FCSTD DOCUMENT  (FreeCAD 0.19R21911 +2545 (Git))
Label: zawieszenie
License: All rights reserved
LicenseURL: http://en.wikipedia.org/wiki/All_rights_reserved
objects: App::Link×4, App::FeaturePython×2, Part::FeaturePython×2
note: 1 computed .brp shape members not serialized (recipe doc carries the construction recipe); baked Part::Feature solids carry a one-line shape summary decoded from their .brp
EXTERNAL_REF file=zawieszenie-dol.fcstd obj=Assembly
EXTERNAL_REF file=zawieszenia-gora.fcstd obj=Assembly

FEATURE [App::FeaturePython] Constraints  # WARN: FeaturePython — macro-defined, semantics opaque (R4)
  _LinkVersion = 1
  _Version = 1
FEATURE [App::FeaturePython] Elements  # WARN: FeaturePython — macro-defined, semantics opaque (R4)
  _LinkVersion = 1
FEATURE [App::Link] Link  label="Link_zawieszenie-dol"
  LinkPlacement = pos=(0.000376772,73.4466,183.14) rot=(0,0,1;0rad)
  LinkedObject = -> <external zawieszenie-dol.fcstd>#Assembly
  Placement = pos=(0.000376772,73.4466,183.14) rot=(0,0,1;0rad)
  SyncGroupVisibility = false
  _LinkVersion = 1
FEATURE [App::Link] Link001  label="Link001_Assembly"
  LinkedObject = -> Assembly
  SyncGroupVisibility = false
  _LinkVersion = 1
FEATURE [App::Link] Link002  label="Link002_zawieszenie-gora"
  LinkPlacement = pos=(0.000381473,73.4466,203.14) rot=(0,0,1;0rad)
  LinkedObject = -> <external zawieszenia-gora.fcstd>#Assembly
  Placement = pos=(0.000381473,73.4466,203.14) rot=(0,0,1;0rad)
  SyncGroupVisibility = false
  _LinkVersion = 1
FEATURE [Part::FeaturePython] Parts  # WARN: FeaturePython — macro-defined, semantics opaque (R4)
  Group = -> [Link,Link002]
  GroupMode = 0
  _LinkVersion = 1
FEATURE [Part::FeaturePython] Assembly  # WARN: FeaturePython — macro-defined, semantics opaque (R4)
  AutoRelax = true
  BuildShape = 0
  Freeze = false
  Group = -> [Constraints,Elements,Parts]
  Verbose = false
  _LinkVersion = 1
  _SolverType = 1
FEATURE [App::Link] Link003  label="Link003_Assembly"
  LinkedObject = -> Assembly
  SyncGroupVisibility = false
  _LinkVersion = 1

RESOLVED EXTERNAL PARTS (link-assembly join: the EXTERNAL_REF files above that resolve inside this repo's crawl, each included once):
---- part zawieszenia-gora.fcstd = doc fcstd_c8abc18c9d7d (55000 chars; too large to inline — full recipe in that document) ----
---- part zawieszenie-dol.fcstd = doc fcstd_90b82e9d4289 ----
FCSTD DOCUMENT  (FreeCAD 2020.12.13R23076 +3015 (Git))
Label: zawieszenie-dol
License: All rights reserved
LicenseURL: http://en.wikipedia.org/wiki/All_rights_reserved
objects: App::FeaturePython×64, Part::FeaturePython×34, App::Link×12, App::LinkElement×6
note: 33 computed .brp shape members not serialized (recipe doc carries the construction recipe); baked Part::Feature solids carry a one-line shape summary decoded from their .brp
EXTERNAL_REF file=plyta-okr-dol.fcstd obj=Body
EXTERNAL_REF file=stopa.fcstd obj=Body
EXTERNAL_REF file=wieniec_mod1.FCStd obj=Body
EXTERNAL_REF file=tulejka-sruby.FCStd obj=Body
EXTERNAL_REF file=piasta-lozyska.FCStd obj=Body
EXTERNAL_REF file=lozysko 51126.FCStd obj=Assembly
EXTERNAL_REF file=regulacja-nogi.FCStd obj=Assembly

FEATURE [App::Link] Link  label="Link_plyta-okr-dol"
  LinkedObject = -> <external plyta-okr-dol.fcstd>#Body
  SyncGroupVisibility = false
  _LinkVersion = 1
FEATURE [App::Link] Link001  label="Link001_Assembly"
  LinkedObject = -> Assembly
  SyncGroupVisibility = false
  _LinkVersion = 1
FEATURE [App::Link] Link002  label="Link002_stopa"
  LinkPlacement = pos=(235,0,0) rot=(0,0,1;0rad)
  LinkedObject = -> <external stopa.fcstd>#Body
  Placement = pos=(235,0,0) rot=(0,0,1;0rad)
  SyncGroupVisibility = false
  _LinkVersion = 1
FEATURE [App::Link] Link003  label="Link003_Assembly"
  LinkedObject = -> Assembly
  SyncGroupVisibility = false
  _LinkVersion = 1
FEATURE [App::Link] Link004  label="Link004_Assembly"
  LinkedObject = -> Assembly
  SyncGroupVisibility = false
  _LinkVersion = 1
FEATURE [App::Link] Link005  label="Link005_stopa"
  LinkPlacement = pos=(-117.5,203.516,0) rot=(0,0,1;0rad)
  LinkedObject = -> <external stopa.fcstd>#Body
  Placement = pos=(-117.5,203.516,0) rot=(0,0,1;0rad)
  SyncGroupVisibility = false
  _LinkVersion = 1
FEATURE [App::Link] Link006  label="Link006_stopa"
  LinkPlacement = pos=(-117.5,-203.516,0) rot=(0,0,1;0rad)
  LinkedObject = -> <external stopa.fcstd>#Body
  Placement = pos=(-117.5,-203.516,0) rot=(0,0,1;0rad)
  SyncGroupVisibility = false
  _LinkVersion = 1
FEATURE [App::Link] Link008  label="tulejka-sruby"
  LinkPlacement = pos=(0,0,-4.40707e-10) rot=(0,0,1;0rad)
  LinkedObject = -> <external tulejka-sruby.FCStd>#Body
  Placement = pos=(0,0,-4.40707e-10) rot=(0,0,1;0rad)
  SyncGroupVisibility = false
  _LinkVersion = 1
FEATURE [App::Link] Link009  label="piasta-lozyska"
  LinkPlacement = pos=(0,0,18) rot=(0,0,1;0rad)
  LinkedObject = -> <external piasta-lozyska.FCStd>#Body
  Placement = pos=(0,0,18) rot=(0,0,1;0rad)
  SyncGroupVisibility = false
  _LinkVersion = 1
FEATURE [App::Link] Link010  label="51126-lozysko"
  LinkPlacement = pos=(0,0,18) rot=(0,-1,0;1.5708rad)
  LinkedObject = -> <external lozysko 51126.FCStd>#Assembly
  Placement = pos=(0,0,18) rot=(0,-1,0;1.5708rad)
  SyncGroupVisibility = false
  _LinkVersion = 1
FEATURE [App::LinkElement] Link011_i0
  LinkPlacement = pos=(0,0,1.8261e-12) rot=(0,0,1;0rad)
  LinkedObject = -> <external regulacja-nogi.FCStd>#Assembly
  Placement = pos=(0,0,1.8261e-12) rot=(0,0,1;0rad)
  _LinkVersion = 1
FEATURE [App::LinkElement] Link011_i1
  LinkPlacement = pos=(-203.516,-352.5,1.8296e-12) rot=(0,0,-1;1.0472rad)
  LinkedObject = -> <external regulacja-nogi.FCStd>#Assembly
  Placement = pos=(-203.516,-352.5,1.8296e-12) rot=(0,0,-1;1.0472rad)
  _LinkVersion = 1
FEATURE [App::LinkElement] Link011_i2
  LinkPlacement = pos=(203.516,-352.5,1.8296e-12) rot=(0,0,1;1.0472rad)
  LinkedObject = -> <external regulacja-nogi.FCStd>#Assembly
  Placement = pos=(203.516,-352.5,1.8296e-12) rot=(0,0,1;1.0472rad)
  _LinkVersion = 1
FEATURE [App::Link] Link011  label="regulacja-nogi"
  ElementCount = 3
  ElementList = -> [Link011_i0,Link011_i1,Link011_i2]
  LinkPlacement = pos=(235,0,-20) rot=(0.707107,0.707107,0;3.14159rad)
  LinkedObject = -> <external regulacja-nogi.FCStd>#Assembly
  Placement = pos=(235,0,-20) rot=(0.707107,0.707107,0;3.14159rad)
  SyncGroupVisibility = false
  _LinkVersion = 1
FEATURE [App::LinkElement] Link007_i0
  LinkPlacement = pos=(0,0,-3.6e-15) rot=(0,0,-1;5.65256rad)
  LinkedObject = -> <external wieniec_mod1.FCStd>#Body
  Placement = pos=(0,0,-3.6e-15) rot=(0,0,-1;5.65256rad)
  _LinkVersion = 0
FEATURE [App::LinkElement] Link007_i1
  LinkPlacement = pos=(2e-16,8e-16,3.6e-15) rot=(0,0,-1;4.77196rad)
  LinkedObject = -> <external wieniec_mod1.FCStd>#Body
  Placement = pos=(2e-16,8e-16,3.6e-15) rot=(0,0,-1;4.77196rad)
  _LinkVersion = 0
FEATURE [App::LinkElement] Link007_i2
  LinkPlacement = pos=(-1.93e-14,2.3e-15,2.49e-14) rot=(0,0,-1;0.249973rad)
  LinkedObject = -> <external wieniec_mod1.FCStd>#Body
  Placement = pos=(-1.93e-14,2.3e-15,2.49e-14) rot=(0,0,-1;0.249973rad)
  _LinkVersion = 0
FEATURE [App::Link] Link007  label="wieniec"
  ElementCount = 3
  ElementList = -> [Link007_i0,Link007_i1,Link007_i2]
  LinkPlacement = pos=(0,0,22) rot=(0.991445,-0.130526,0;3.14159rad)
  LinkedObject = -> <external wieniec_mod1.FCStd>#Body
  Placement = pos=(0,0,22) rot=(0.991445,-0.130526,0;3.14159rad)
  SyncGroupVisibility = false
  _LinkVersion = 1
FEATURE [Part::FeaturePython] Parts  # WARN: FeaturePython — macro-defined, semantics opaque (R4)
  Group = -> [Link,Link002,Link005,Link006,Link007,Link008,Link009,Link010,Link011]
  GroupMode = 0
  _LinkVersion = 1
FEATURE [Part::FeaturePython] Assembly  label="zawieszenie-dol"  # WARN: FeaturePython — macro-defined, semantics opaque (R4)
  AutoRelax = true
  BuildShape = 0
  Freeze = true
  Group = -> [Constraints,Elements,Parts]
  Verbose = false
  _LinkVersion = 1
  _SolverType = 1
FEATURE [App::FeaturePython] Constraints  # WARN: FeaturePython — macro-defined, semantics opaque (R4)
  Group = -> [Constraint001,Constraint002,Constraint003,Constraint004,Constraint005,Constraint006,Constraint,Constraint011,Constraint012,Constraint013,Constraint014,Constraint015,Constraint016,Constraint017,Constraint018,Constraint019,Constraint020,Constraint021,Constraint022,Constraint023,Constraint024]
  _LinkVersion = 1
  _Version = 1
FEATURE [App::FeaturePython] Elements  # WARN: FeaturePython — macro-defined, semantics opaque (R4)
  Group = -> [_Element,_Element001,_Element002,_Element003,_Element004,_Element005,_Element006,_Element007,_Element008,_Element009,_Element011,_Element013,_Element015,_Element017,Element,Element001,_Element018,_Element019,_Element020,_Element021,_Element022,_Element023,_Element024,_Element025,_Element026,_Element027,_Element028,_Element029,_Element030,_Element031,_Element032,_Element033]
  _LinkVersion = 1
FEATURE [Part::FeaturePython] _Element  # link proxy (typed FeaturePython)
  Detach = false
  LinkTransform = true
  LinkedObject = -> Link [PolarPattern.Face2]
  _LinkVersion = 1
  _Parent = -> Elements
FEATURE [App::FeaturePython] Constraint001  label="AxialAlignment"  # WARN: FeaturePython — macro-defined, semantics opaque (R4)
  Angle = 0
  AnglePitch = 0
  AngleRoll = 0
  Disabled = false
  Group = -> [ElementLink001,ElementLink002]
  LockAngle = false
  Multiply = false
  _ConstraintType = 36
  _LinkVersion = 1
  _Parent = -> Constraints
FEATURE [App::FeaturePython] ElementLink001  label="_Element001"  # link proxy (typed FeaturePython)
  LinkTransform = true
  LinkedObject = -> _Element001
  _LinkVersion = 1
  _Parent = -> Constraint001
FEATURE [Part::FeaturePython] _Element001  # link proxy (typed FeaturePython)
  Detach = false
  LinkTransform = true
  LinkedObject = -> Link005 [Revolution.Edge1]
  _LinkVersion = 1
  _Parent = -> Elements
FEATURE [App::FeaturePython] ElementLink002  label="_Element002"  # link proxy (typed FeaturePython)
  LinkTransform = true
  LinkedObject = -> _Element002
  _LinkVersion = 1
  _Parent = -> Constraint001
FEATURE [Part::FeaturePython] _Element002  # link proxy (typed FeaturePython)
  Detach = false
  LinkTransform = true
  LinkedObject = -> Link [PolarPattern.Edge6]
  _LinkVersion = 1
  _Parent = -> Elements
FEATURE [App::FeaturePython] Constraint002  label="PlaneAlignment"  # WARN: FeaturePython — macro-defined, semantics opaque (R4)
  Angle = 0
  AnglePitch = 0
  AngleRoll = 0
  Cascade = false
  Disabled = false
  Group = -> [ElementLink003,ElementLink004]
  LockAngle = false
  _ConstraintType = 37
  _LinkVersion = 1
  _Parent = -> Constraints
FEATURE [App::FeaturePython] ElementLink003  label="_Element"  # link proxy (typed FeaturePython)
  LinkTransform = true
  LinkedObject = -> _Element
  _LinkVersion = 1
  _Parent = -> Constraint002
FEATURE [App::FeaturePython] ElementLink004  label="_Element003"  # link proxy (typed FeaturePython)
  LinkTransform = true
  LinkedObject = -> _Element003
  _LinkVersion = 1
  _Parent = -> Constraint002
FEATURE [Part::FeaturePython] _Element003  # link proxy (typed FeaturePython)
  Detach = false
  LinkTransform = true
  LinkedObject = -> Link005 [Revolution.Face1]
  _LinkVersion = 1
  _Parent = -> Elements
FEATURE [App::FeaturePython] Constraint003  label="AxialAlignment001"  # WARN: FeaturePython — macro-defined, semantics opaque (R4)
  Angle = 0
  AnglePitch = 0
  AngleRoll = 0
  Disabled = false
  Group = -> [ElementLink005,ElementLink006]
  LockAngle = false
  Multiply = false
  _ConstraintType = 36
  _LinkVersion = 1
  _Parent = -> Constraints
FEATURE [App::FeaturePython] ElementLink005  label="_Element004"  # link proxy (typed FeaturePython)
  LinkTransform = true
  LinkedObject = -> _Element004
  _LinkVersion = 1
  _Parent = -> Constraint003
FEATURE [Part::FeaturePython] _Element004  # link proxy (typed FeaturePython)
  Detach = false
  LinkTransform = true
  LinkedObject = -> Link006 [Revolution.Edge1]
  _LinkVersion = 1
  _Parent = -> Elements
FEATURE [App::FeaturePython] ElementLink006  label="_Element005"  # link proxy (typed FeaturePython)
  LinkTransform = true
  LinkedObject = -> _Element005
  _LinkVersion = 1
  _Parent = -> Constraint003
FEATURE [Part::FeaturePython] _Element005  # link proxy (typed FeaturePython)
  Detach = false
  LinkTransform = true
  LinkedObject = -> Link [PolarPattern.Edge4]
  _LinkVersion = 1
  _Parent = -> Elements
FEATURE [App::FeaturePython] Constraint004  label="PlaneAlignment001"  # WARN: FeaturePython — macro-defined, semantics opaque (R4)
  Angle = 0
  AnglePitch = 0
  AngleRoll = 0
  Cascade = false
  Disabled = false
  Group = -> [ElementLink007,ElementLink008]
  LockAngle = false
  _ConstraintType = 37
  _LinkVersion = 1
  _Parent = -> Constraints
FEATURE [App::FeaturePython] ElementLink007  label="_Element"  # link proxy (typed FeaturePython)
  LinkTransform = true
  LinkedObject = -> _Element
  _LinkVersion = 1
  _Parent = -> Constraint004
FEATURE [App::FeaturePython] ElementLink008  label="_Element006"  # link proxy (typed FeaturePython)
  LinkTransform = true
  LinkedObject = -> _Element006
  _LinkVersion = 1
  _Parent = -> Constraint004
FEATURE [Part::FeaturePython] _Element006  # link proxy (typed FeaturePython)
  Detach = false
  LinkTransform = true
  LinkedObject = -> Link006 [Revolution.Face1]
  _LinkVersion = 1
  _Parent = -> Elements
FEATURE [App::FeaturePython] Constraint005  label="AxialAlignment002"  # WARN: FeaturePython — macro-defined, semantics opaque (R4)
  Angle = 0
  AnglePitch = 0
  AngleRoll = 0
  Disabled = false
  Group = -> [ElementLink009,ElementLink010]
  LockAngle = false
  Multiply = false
  _ConstraintType = 36
  _LinkVersion = 1
  _Parent = -> Constraints
FEATURE [App::FeaturePython] ElementLink009  label="_Element007"  # link proxy (typed FeaturePython)
  LinkTransform = true
  LinkedObject = -> _Element007
  _LinkVersion = 1
  _Parent = -> Constraint005
FEATURE [Part::FeaturePython] _Element007  # link proxy (typed FeaturePython)
  Detach = false
  LinkTransform = true
  LinkedObject = -> Link002 [Revolution.Edge1]
  _LinkVersion = 1
  _Parent = -> Elements
FEATURE [App::FeaturePython] ElementLink010  label="_Element008"  # link proxy (typed FeaturePython)
  LinkTransform = true
  LinkedObject = -> _Element008
  _LinkVersion = 1
  _Parent = -> Constraint005
FEATURE [Part::FeaturePython] _Element008  # link proxy (typed FeaturePython)
  Detach = false
  LinkTransform = true
  LinkedObject = -> Link [PolarPattern.Edge5]
  _LinkVersion = 1
  _Parent = -> Elements
FEATURE [App::FeaturePython] Constraint006  label="PlaneAlignment002"  # WARN: FeaturePython — macro-defined, semantics opaque (R4)
  Angle = 0
  AnglePitch = 0
  AngleRoll = 0
  Cascade = false
  Disabled = false
  Group = -> [ElementLink011,ElementLink012]
  LockAngle = false
  _ConstraintType = 37
  _LinkVersion = 1
  _Parent = -> Constraints
FEATURE [App::FeaturePython] ElementLink011  label="_Element"  # link proxy (typed FeaturePython)
  LinkTransform = true
  LinkedObject = -> _Element
  _LinkVersion = 1
  _Parent = -> Constraint006
FEATURE [App::FeaturePython] ElementLink012  label="_Element009"  # link proxy (typed FeaturePython)
  LinkTransform = true
  LinkedObject = -> _Element009
  _LinkVersion = 1
  _Parent = -> Constraint006
FEATURE [Part::FeaturePython] _Element009  # link proxy (typed FeaturePython)
  Detach = false
  LinkTransform = true
  LinkedObject = -> Link002 [Revolution.Face1]
  _LinkVersion = 1
  _Parent = -> Elements
FEATURE [Part::FeaturePython] _Element011  # link proxy (typed FeaturePython)
  Detach = false
  LinkTransform = true
  LinkedObject = -> Link [PolarPattern.Face1]
  _LinkVersion = 1
  _Parent = -> Elements
FEATURE [Part::FeaturePython] _Element013  # link proxy (typed FeaturePython)
  Detach = false
  LinkTransform = true
  LinkedObject = -> Link [PolarPattern.Face3]
  _LinkVersion = 1
  _Parent = -> Elements
FEATURE [Part::FeaturePython] _Element015  # link proxy (typed FeaturePython)
  Detach = false
  LinkTransform = true
  LinkedObject = -> Link [Pocket001.Face1]
  _LinkVersion = 1
  _Parent = -> Elements
FEATURE [Part::FeaturePython] _Element017  # link proxy (typed FeaturePython)
  Detach = false
  LinkTransform = true
  LinkedObject = -> Link [Pocket001.Face3]
  _LinkVersion = 1
  _Parent = -> Elements
FEATURE [Part::FeaturePython] Element  # link proxy (typed FeaturePython)
  Detach = false
  LinkTransform = true
  LinkedObject = -> Link [Pocket001.Face5]
  _LinkVersion = 1
  _Parent = -> Elements
FEATURE [Part::FeaturePython] Element001  # link proxy (typed FeaturePython)
  Detach = false
  LinkTransform = true
  LinkedObject = -> Link [Pocket001.Edge5]
  _LinkVersion = 1
  _Parent = -> Elements
FEATURE [App::FeaturePython] Constraint  label="Locked"  # WARN: FeaturePython — macro-defined, semantics opaque (R4)
  Disabled = false
  Group = -> [ElementLink]
  _ConstraintType = 0
  _LinkVersion = 1
  _Parent = -> Constraints
FEATURE [App::FeaturePython] ElementLink  label="_Element018"  # link proxy (typed FeaturePython)
  LinkTransform = true
  LinkedObject = -> _Element018
  _LinkVersion = 1
  _Parent = -> Constraint
FEATURE [Part::FeaturePython] _Element018  # link proxy (typed FeaturePython)
  Detach = false
  LinkTransform = true
  LinkedObject = -> Link [Pocket001.Face2]
  _LinkVersion = 1
  _Parent = -> Elements
FEATURE [Part::FeaturePython] _Element019  # link proxy (typed FeaturePython)
  Detach = false
  LinkTransform = true
  LinkedObject = -> Link008 [Chamfer.Face1]
  _LinkVersion = 1
  _Parent = -> Elements
FEATURE [Part::FeaturePython] _Element020  # link proxy (typed FeaturePython)
  Detach = false
  LinkTransform = true
  LinkedObject = -> Link008 [Chamfer.Face3]
  _LinkVersion = 1
  _Parent = -> Elements
FEATURE [App::FeaturePython] Constraint011  label="PlaneCoincident"  # WARN: FeaturePython — macro-defined, semantics opaque (R4)
  Angle = 0
  AnglePitch = 0
  AngleRoll = 0
  Cascade = false
  Disabled = false
  Group = -> [ElementLink021,ElementLink022]
  LockAngle = false
  Multiply = false
  OffsetX = 0
  OffsetY = 0
  _ConstraintType = 35
  _LinkVersion = 1
  _Parent = -> Constraints
FEATURE [App::FeaturePython] ElementLink021  label="_Element021"  # link proxy (typed FeaturePython)
  LinkTransform = true
  LinkedObject = -> _Element021
  _LinkVersion = 1
  _Parent = -> Constraint011
FEATURE [Part::FeaturePython] _Element021  # link proxy (typed FeaturePython)
  Detach = false
  LinkTransform = true
  LinkedObject = -> Link009 [Pocket002.Face1]
  _LinkVersion = 1
  _Parent = -> Elements
FEATURE [App::FeaturePython] ElementLink022  label="_Element017"  # link proxy (typed FeaturePython)
  LinkTransform = true
  LinkedObject = -> _Element017
  _LinkVersion = 1
  _Parent = -> Constraint011
FEATURE [App::FeaturePython] Constraint012  label="PlaneCoincident001"  # WARN: FeaturePython — macro-defined, semantics opaque (R4)
  Angle = 0
  AnglePitch = 0
  AngleRoll = 0
  Cascade = false
  Disabled = false
  Group = -> [ElementLink023,ElementLink024]
  LockAngle = false
  Multiply = false
  OffsetX = 0
  OffsetY = 0
  _ConstraintType = 35
  _LinkVersion = 1
  _Parent = -> Constraints
FEATURE [App::FeaturePython] ElementLink023  label="_Element020"  # link proxy (typed FeaturePython)
  LinkTransform = true
  LinkedObject = -> _Element020
  _LinkVersion = 1
  _Parent = -> Constraint012
FEATURE [App::FeaturePython] ElementLink024  label="_Element018"  # link proxy (typed FeaturePython)
  LinkTransform = true
  LinkedObject = -> _Element018
  _LinkVersion = 1
  _Parent = -> Constraint012
FEATURE [App::FeaturePython] Constraint013  label="PlaneCoincident002"  # WARN: FeaturePython — macro-defined, semantics opaque (R4)
  Angle = 0
  AnglePitch = 0
  AngleRoll = 0
  Cascade = false
  Disabled = false
  Group = -> [ElementLink025,ElementLink026]
  LockAngle = false
  Multiply = false
  OffsetX = 0
  OffsetY = 0
  _ConstraintType = 35
  _LinkVersion = 1
  _Parent = -> Constraints
FEATURE [App::FeaturePython] ElementLink025  label="_Element022"  # link proxy (typed FeaturePython)
  LinkTransform = true
  LinkedObject = -> _Element022
  _LinkVersion = 1
  _Parent = -> Constraint013
FEATURE [Part::FeaturePython] _Element022  # link proxy (typed FeaturePython)
  Detach = false
  LinkTransform = true
  LinkedObject = -> Link010 [1.$Element.]
  _LinkVersion = 1
  _Parent = -> Elements
FEATURE [App::FeaturePython] ElementLink026  label="_Element017"  # link proxy (typed FeaturePython)
  LinkTransform = true
  LinkedObject = -> _Element017
  _LinkVersion = 1
  _Parent = -> Constraint013
FEATURE [Part::FeaturePython] _Element023  # link proxy (typed FeaturePython)
  Detach = false
  LinkTransform = true
  LinkedObject = -> Link [Pocket001.Edge6]
  _LinkVersion = 1
  _Parent = -> Elements
FEATURE [App::FeaturePython] Constraint014  label="PlaneCoincident003"  # WARN: FeaturePython — macro-defined, semantics opaque (R4)
  Angle = 0
  AnglePitch = 0
  AngleRoll = 0
  Cascade = false
  Disabled = false
  Group = -> [ElementLink027,ElementLink028]
  LockAngle = false
  Multiply = false
  OffsetX = 0
  OffsetY = 0
  _ConstraintType = 35
  _LinkVersion = 1
  _Parent = -> Constraints
FEATURE [App::FeaturePython] ElementLink027  label="_Element024"  # link proxy (typed FeaturePython)
  LinkTransform = true
  LinkedObject = -> _Element024
  _LinkVersion = 1
  _Parent = -> Constraint014
FEATURE [Part::FeaturePython] _Element024  # link proxy (typed FeaturePython)
  Detach = false
  LinkTransform = true
  LinkedObject = -> Link011 [0.1.$Element002.]
  _LinkVersion = 1
  _Parent = -> Elements
FEATURE [App::FeaturePython] ElementLink028  label="_Element009"  # link proxy (typed FeaturePython)
  LinkTransform = true
  LinkedObject = -> _Element009
  _LinkVersion = 1
  _Parent = -> Constraint014
FEATURE [App::FeaturePython] Constraint015  label="PlaneCoincident004"  # WARN: FeaturePython — macro-defined, semantics opaque (R4)
  Angle = 0
  AnglePitch = 0
  AngleRoll = 0
  Cascade = false
  Disabled = false
  Group = -> [ElementLink029,ElementLink030]
  LockAngle = false
  Multiply = false
  OffsetX = 0
  OffsetY = 0
  _ConstraintType = 35
  _LinkVersion = 1
  _Parent = -> Constraints
FEATURE [App::FeaturePython] ElementLink029  label="_Element025"  # link proxy (typed FeaturePython)
  LinkTransform = true
  LinkedObject = -> _Element025
  _LinkVersion = 1
  _Parent = -> Constraint015
FEATURE [Part::FeaturePython] _Element025  # link proxy (typed FeaturePython)
  Detach = false
  LinkTransform = true
  LinkedObject = -> Link011 [2.1.$Element002.]
  _LinkVersion = 1
  _Parent = -> Elements
FEATURE [App::FeaturePython] ElementLink030  label="_Element003"  # link proxy (typed FeaturePython)
  LinkTransform = true
  LinkedObject = -> _Element003
  _LinkVersion = 1
  _Parent = -> Constraint015
FEATURE [App::FeaturePython] Constraint016  label="PlaneCoincident005"  # WARN: FeaturePython — macro-defined, semantics opaque (R4)
  Angle = 0
  AnglePitch = 0
  AngleRoll = 0
  Cascade = false
  Disabled = false
  Group = -> [ElementLink031,ElementLink032]
  LockAngle = false
  Multiply = false
  OffsetX = 0
  OffsetY = 0
  _ConstraintType = 35
  _LinkVersion = 1
  _Parent = -> Constraints
FEATURE [App::FeaturePython] ElementLink031  label="_Element006"  # link proxy (typed FeaturePython)
  LinkTransform = true
  LinkedObject = -> _Element006
  _LinkVersion = 1
  _Parent = -> Constraint016
FEATURE [App::FeaturePython] ElementLink032  label="_Element026"  # link proxy (typed FeaturePython)
  LinkTransform = true
  LinkedObject = -> _Element026
  _LinkVersion = 1
  _Parent = -> Constraint016
FEATURE [Part::FeaturePython] _Element026  # link proxy (typed FeaturePython)
  Detach = false
  LinkTransform = true
  LinkedObject = -> Link011 [1.1.$Element002.]
  _LinkVersion = 1
  _Parent = -> Elements
FEATURE [App::FeaturePython] Constraint017  label="AxialAlignment003"  # WARN: FeaturePython — macro-defined, semantics opaque (R4)
  Angle = 0
  AnglePitch = 0
  AngleRoll = 0
  Disabled = false
  Group = -> [ElementLink033,ElementLink034]
  LockAngle = false
  Multiply = false
  _ConstraintType = 36
  _LinkVersion = 0
  _Parent = -> Constraints
FEATURE [App::FeaturePython] ElementLink033  label="_Element027"  # link proxy (typed FeaturePython)
  LinkTransform = true
  LinkedObject = -> _Element027
  _LinkVersion = 0
  _Parent = -> Constraint017
FEATURE [Part::FeaturePython] _Element027  # link proxy (typed FeaturePython)
  Detach = false
  LinkTransform = true
  LinkedObject = -> Link007 [2.Pocket003.Face3]
  _LinkVersion = 0
  _Parent = -> Elements
FEATURE [App::FeaturePython] ElementLink034  label="_Element015"  # link proxy (typed FeaturePython)
  LinkTransform = true
  LinkedObject = -> _Element015
  _LinkVersion = 0
  _Parent = -> Constraint017
FEATURE [App::FeaturePython] Constraint018  label="AxialAlignment004"  # WARN: FeaturePython — macro-defined, semantics opaque (R4)
  Angle = 0
  AnglePitch = 0
  AngleRoll = 0
  Disabled = false
  Group = -> [ElementLink035,ElementLink036]
  LockAngle = false
  Multiply = false
  _ConstraintType = 36
  _LinkVersion = 0
  _Parent = -> Constraints
FEATURE [App::FeaturePython] ElementLink035  label="_Element028"  # link proxy (typed FeaturePython)
  LinkTransform = true
  LinkedObject = -> _Element028
  _LinkVersion = 0
  _Parent = -> Constraint018
FEATURE [Part::FeaturePython] _Element028  # link proxy (typed FeaturePython)
  Detach = false
  LinkTransform = true
  LinkedObject = -> Link007 [0.Pocket003.Face3]
  _LinkVersion = 0
  _Parent = -> Elements
FEATURE [App::FeaturePython] ElementLink036  label="_Element015"  # link proxy (typed FeaturePython)
  LinkTransform = true
  LinkedObject = -> _Element015
  _LinkVersion = 0
  _Parent = -> Constraint018
FEATURE [App::FeaturePython] Constraint019  label="PointInPlane"  # WARN: FeaturePython — macro-defined, semantics opaque (R4)
  Disabled = false
  Group = -> [ElementLink037,ElementLink038]
  _ConstraintType = 3
  _LinkVersion = 0
  _Parent = -> Constraints
FEATURE [App::FeaturePython] ElementLink037  label="_Element029"  # link proxy (typed FeaturePython)
  LinkTransform = true
  LinkedObject = -> _Element029
  _LinkVersion = 0
  _Parent = -> Constraint019
FEATURE [Part::FeaturePython] _Element029  # link proxy (typed FeaturePython)
  Detach = false
  LinkTransform = true
  LinkedObject = -> Link007 [0.Pocket003.Vertex323]
  _LinkVersion = 0
  _Parent = -> Elements
FEATURE [App::FeaturePython] ElementLink038  label="_Element017"  # link proxy (typed FeaturePython)
  LinkTransform = true
  LinkedObject = -> _Element017
  _LinkVersion = 0
  _Parent = -> Constraint019
FEATURE [App::FeaturePython] Constraint020  label="PointInPlane001"  # WARN: FeaturePython — macro-defined, semantics opaque (R4)
  Disabled = false
  Group = -> [ElementLink039,ElementLink040]
  _ConstraintType = 3
  _LinkVersion = 0
  _Parent = -> Constraints
FEATURE [App::FeaturePython] ElementLink039  label="_Element030"  # link proxy (typed FeaturePython)
  LinkTransform = true
  LinkedObject = -> _Element030
  _LinkVersion = 0
  _Parent = -> Constraint020
FEATURE [Part::FeaturePython] _Element030  # link proxy (typed FeaturePython)
  Detach = false
  LinkTransform = true
  LinkedObject = -> Link007 [2.Pocket003.Vertex325]
  _LinkVersion = 0
  _Parent = -> Elements
FEATURE [App::FeaturePython] ElementLink040  label="_Element017"  # link proxy (typed FeaturePython)
  LinkTransform = true
  LinkedObject = -> _Element017
  _LinkVersion = 0
  _Parent = -> Constraint020
FEATURE [App::FeaturePython] Constraint021  label="PointsCoincident"  # WARN: FeaturePython — macro-defined, semantics opaque (R4)
  Disabled = false
  Group = -> [ElementLink041,ElementLink042]
  _ConstraintType = 1
  _LinkVersion = 0
  _Parent = -> Constraints
FEATURE [App::FeaturePython] ElementLink041  label="_Element030"  # link proxy (typed FeaturePython)
  LinkTransform = true
  LinkedObject = -> _Element030
  _LinkVersion = 0
  _Parent = -> Constraint021
FEATURE [App::FeaturePython] ElementLink042  label="_Element029"  # link proxy (typed FeaturePython)
  LinkTransform = true
  LinkedObject = -> _Element029
  _LinkVersion = 0
  _Parent = -> Constraint021
FEATURE [App::FeaturePython] Constraint022  label="AxialAlignment005"  # WARN: FeaturePython — macro-defined, semantics opaque (R4)
  Angle = 0
  AnglePitch = 0
  AngleRoll = 0
  Disabled = false
  Group = -> [ElementLink043,ElementLink044]
  LockAngle = false
  Multiply = false
  _ConstraintType = 36
  _LinkVersion = 0
  _Parent = -> Constraints
FEATURE [App::FeaturePython] ElementLink043  label="_Element031"  # link proxy (typed FeaturePython)
  LinkTransform = true
  LinkedObject = -> _Element031
  _LinkVersion = 0
  _Parent = -> Constraint022
FEATURE [Part::FeaturePython] _Element031  # link proxy (typed FeaturePython)
  Detach = false
  LinkTransform = true
  LinkedObject = -> Link007 [1.Pocket003.Face3]
  _LinkVersion = 0
  _Parent = -> Elements
FEATURE [App::FeaturePython] ElementLink044  label="_Element015"  # link proxy (typed FeaturePython)
  LinkTransform = true
  LinkedObject = -> _Element015
  _LinkVersion = 0
  _Parent = -> Constraint022
FEATURE [App::FeaturePython] Constraint023  label="PointInPlane002"  # WARN: FeaturePython — macro-defined, semantics opaque (R4)
  Disabled = false
  Group = -> [ElementLink045,ElementLink046]
  _ConstraintType = 3
  _LinkVersion = 0
  _Parent = -> Constraints
FEATURE [App::FeaturePython] ElementLink045  label="_Element032"  # link proxy (typed FeaturePython)
  LinkTransform = true
  LinkedObject = -> _Element032
  _LinkVersion = 0
  _Parent = -> Constraint023
FEATURE [Part::FeaturePython] _Element032  # link proxy (typed FeaturePython)
  Detach = false
  LinkTransform = true
  LinkedObject = -> Link007 [1.Pocket003.Vertex323]
  _LinkVersion = 0
  _Parent = -> Elements
FEATURE [App::FeaturePython] ElementLink046  label="_Element017"  # link proxy (typed FeaturePython)
  LinkTransform = true
  LinkedObject = -> _Element017
  _LinkVersion = 0
  _Parent = -> Constraint023
FEATURE [App::FeaturePython] Constraint024  label="PointsCoincident001"  # WARN: FeaturePython — macro-defined, semantics opaque (R4)
  Disabled = false
  Group = -> [ElementLink047,ElementLink048]
  _ConstraintType = 1
  _LinkVersion = 0
  _Parent = -> Constraints
FEATURE [App::FeaturePython] ElementLink047  label="_Element032"  # link proxy (typed FeaturePython)
  LinkTransform = true
  LinkedObject = -> _Element032
  _LinkVersion = 0
  _Parent = -> Constraint024
FEATURE [App::FeaturePython] ElementLink048  label="_Element033"  # link proxy (typed FeaturePython)
  LinkTransform = true
  LinkedObject = -> _Element033
  _LinkVersion = 0
  _Parent = -> Constraint024
FEATURE [Part::FeaturePython] _Element033  # link proxy (typed FeaturePython)
  Detach = false
  LinkTransform = true
  LinkedObject = -> Link007 [0.Pocket003.Vertex325]
  _LinkVersion = 0
  _Parent = -> Elements
